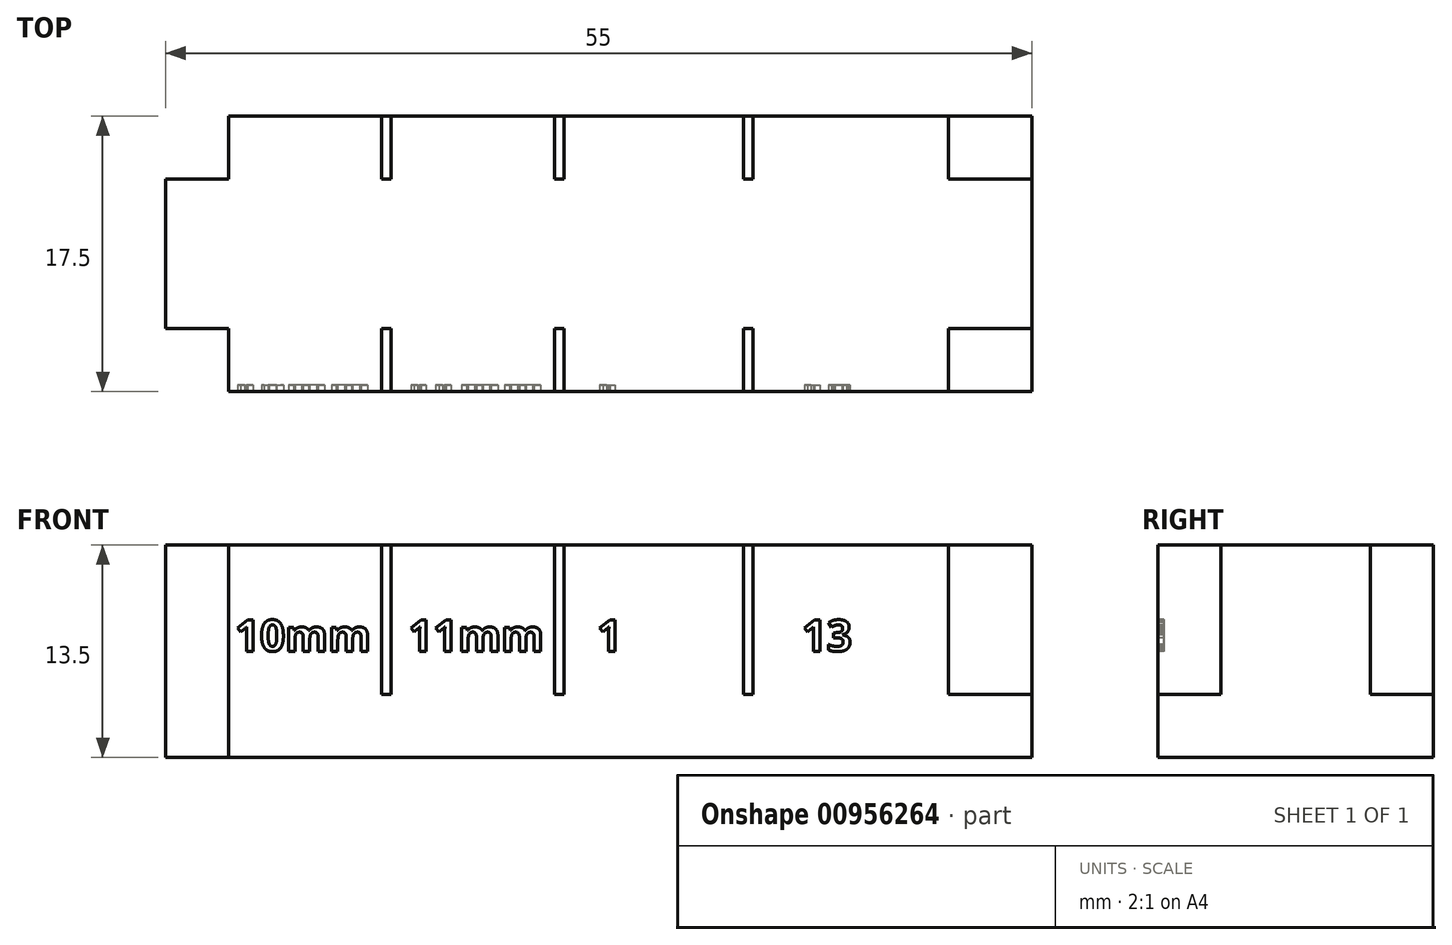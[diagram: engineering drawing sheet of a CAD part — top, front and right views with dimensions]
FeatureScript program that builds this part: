
annotation { "Feature Type Name" : "Feature", "Feature Type Description" : "" }
export const myFeature = defineFeature(function(context is Context, id is Id, definition is map)
    precondition{}
    {
        {
            var Q0;
            Q0=qCreatedBy(makeId("Top.planeOp"),FACE);
            var sketch = newSketch(context, id + "F0", { "sketchPlane" : qUnion([Q0])});
            skLineSegment(sketch, "E0.bottom", {"start": v(-8.23, -5.67) * mm, "end": v(46.77, -5.67) * mm});
            skLineSegment(sketch, "E0.top", {"start": v(-8.23, -23.17) * mm, "end": v(46.77, -23.17) * mm});
            skLineSegment(sketch, "E0.left", {"start": v(-8.23, -5.67) * mm, "end": v(-8.23, -23.17) * mm});
            skLineSegment(sketch, "E0.right", {"start": v(46.77, -5.67) * mm, "end": v(46.77, -23.17) * mm});
            skLineSegment(sketch, "E1.top", {"start": v(-8.23, -9.67) * mm, "end": v(46.77, -9.67) * mm});
            skLineSegment(sketch, "E1.left", {"start": v(-8.23, -5.67) * mm, "end": v(-8.23, -9.67) * mm});
            skLineSegment(sketch, "E1.right", {"start": v(46.77, -5.67) * mm, "end": v(46.77, -9.67) * mm});
            skLineSegment(sketch, "E2.top", {"start": v(-8.23, -19.17) * mm, "end": v(46.77, -19.17) * mm});
            skLineSegment(sketch, "E2.left", {"start": v(-8.23, -23.17) * mm, "end": v(-8.23, -19.17) * mm});
            skLineSegment(sketch, "E2.right", {"start": v(46.77, -23.17) * mm, "end": v(46.77, -19.17) * mm});
            skLineSegment(sketch, "E3.bottom", {"start": v(-8.23, -5.67) * mm, "end": v(-4.23, -5.67) * mm});
            skLineSegment(sketch, "E3.top", {"start": v(-8.23, -23.17) * mm, "end": v(-4.23, -23.17) * mm});
            skLineSegment(sketch, "E3.right", {"start": v(-4.23, -5.67) * mm, "end": v(-4.23, -23.17) * mm});
            skLineSegment(sketch, "E4", {"start": v(5.77, -5.67) * mm, "end": v(5.77, -23.17) * mm});
            skLineSegment(sketch, "E5", {"start": v(16.77, -5.67) * mm, "end": v(16.77, -23.17) * mm});
            skLineSegment(sketch, "E6", {"start": v(28.77, -5.67) * mm, "end": v(28.77, -23.17) * mm});
            skLineSegment(sketch, "E7", {"start": v(41.77, -5.67) * mm, "end": v(41.77, -23.17) * mm});
            skLineSegment(sketch, "E8.bottom", {"start": v(5.47, -5.67) * mm, "end": v(6.07, -5.67) * mm});
            skLineSegment(sketch, "E8.top", {"start": v(5.47, -23.17) * mm, "end": v(6.07, -23.17) * mm});
            skLineSegment(sketch, "E8.left", {"start": v(5.47, -5.67) * mm, "end": v(5.47, -23.17) * mm});
            skLineSegment(sketch, "E8.right", {"start": v(6.07, -5.67) * mm, "end": v(6.07, -23.17) * mm});
            skPoint(sketch, "E8.middle", {"position": v(5.77, -14.42) * mm});
            skLineSegment(sketch, "E9.bottom", {"start": v(16.47, -5.67) * mm, "end": v(17.07, -5.67) * mm});
            skLineSegment(sketch, "E9.top", {"start": v(16.47, -23.17) * mm, "end": v(17.07, -23.17) * mm});
            skLineSegment(sketch, "E9.left", {"start": v(16.47, -5.67) * mm, "end": v(16.47, -23.17) * mm});
            skLineSegment(sketch, "E9.right", {"start": v(17.07, -5.67) * mm, "end": v(17.07, -23.17) * mm});
            skPoint(sketch, "E9.middle", {"position": v(16.77, -14.42) * mm});
            skLineSegment(sketch, "E10.bottom", {"start": v(28.47, -5.67) * mm, "end": v(29.07, -5.67) * mm});
            skLineSegment(sketch, "E10.top", {"start": v(28.47, -23.17) * mm, "end": v(29.07, -23.17) * mm});
            skLineSegment(sketch, "E10.left", {"start": v(28.47, -5.67) * mm, "end": v(28.47, -23.17) * mm});
            skLineSegment(sketch, "E10.right", {"start": v(29.07, -5.67) * mm, "end": v(29.07, -23.17) * mm});
            skPoint(sketch, "E10.middle", {"position": v(28.77, -14.42) * mm});
            skLineSegment(sketch, "E11.bottom", {"start": v(41.47, -5.67) * mm, "end": v(42.07, -5.67) * mm});
            skLineSegment(sketch, "E11.top", {"start": v(41.47, -23.17) * mm, "end": v(42.07, -23.17) * mm});
            skLineSegment(sketch, "E11.left", {"start": v(41.47, -5.67) * mm, "end": v(41.47, -23.17) * mm});
            skLineSegment(sketch, "E11.right", {"start": v(42.07, -5.67) * mm, "end": v(42.07, -23.17) * mm});
            skPoint(sketch, "E11.middle", {"position": v(41.77, -14.42) * mm});
            skSolve(sketch);
        }
        {
            var Q0;
            {var subQ0=sQuery(id+"F0.wireOp",EDGE,"E3.right");var subQ1=sQuery(id+"F0.wireOp",EDGE,"E1.top");var subQ2=makeQuery(id+"F0.imprint","INTERSECT",VERTEX,{"derivedFrom":[subQ1,subQ0]});Q0=makeQuery(id+"F0.imprint","IMPRINT",FACE,{"disambiguationData":[TD([[makeQuery(id+"F0.imprint","IMPRINT",EDGE,{"disambiguationData":[TD([[subQ2,-1.0]])],"derivedFrom":subQ1}),-1.0]])]});}
            var Q1;
            {var subQ0=sQuery(id+"F0.wireOp",EDGE,"E8.left");var subQ1=sQuery(id+"F0.wireOp",EDGE,"E1.top");var subQ2=makeQuery(id+"F0.imprint","INTERSECT",VERTEX,{"derivedFrom":[subQ1,subQ0]});Q1=makeQuery(id+"F0.imprint","IMPRINT",FACE,{"disambiguationData":[TD([[makeQuery(id+"F0.imprint","IMPRINT",EDGE,{"disambiguationData":[TD([[subQ2,-1.0]])],"derivedFrom":subQ1}),-1.0]])]});}
            var Q2;
            {var subQ0=sQuery(id+"F0.wireOp",EDGE,"E4");var subQ1=sQuery(id+"F0.wireOp",EDGE,"E1.top");var subQ2=makeQuery(id+"F0.imprint","INTERSECT",VERTEX,{"derivedFrom":[subQ1,subQ0]});Q2=makeQuery(id+"F0.imprint","IMPRINT",FACE,{"disambiguationData":[TD([[makeQuery(id+"F0.imprint","IMPRINT",EDGE,{"disambiguationData":[TD([[subQ2,-1.0]])],"derivedFrom":subQ1}),-1.0]])]});}
            var Q3;
            {var subQ0=sQuery(id+"F0.wireOp",EDGE,"E8.right");var subQ1=sQuery(id+"F0.wireOp",EDGE,"E1.top");var subQ2=makeQuery(id+"F0.imprint","INTERSECT",VERTEX,{"derivedFrom":[subQ1,subQ0]});Q3=makeQuery(id+"F0.imprint","IMPRINT",FACE,{"disambiguationData":[TD([[makeQuery(id+"F0.imprint","IMPRINT",EDGE,{"disambiguationData":[TD([[subQ2,-1.0]])],"derivedFrom":subQ1}),-1.0]])]});}
            var Q4;
            {var subQ0=sQuery(id+"F0.wireOp",EDGE,"E9.left");var subQ1=sQuery(id+"F0.wireOp",EDGE,"E1.top");var subQ2=makeQuery(id+"F0.imprint","INTERSECT",VERTEX,{"derivedFrom":[subQ1,subQ0]});Q4=makeQuery(id+"F0.imprint","IMPRINT",FACE,{"disambiguationData":[TD([[makeQuery(id+"F0.imprint","IMPRINT",EDGE,{"disambiguationData":[TD([[subQ2,-1.0]])],"derivedFrom":subQ1}),-1.0]])]});}
            var Q5;
            {var subQ0=sQuery(id+"F0.wireOp",EDGE,"E5");var subQ1=sQuery(id+"F0.wireOp",EDGE,"E1.top");var subQ2=makeQuery(id+"F0.imprint","INTERSECT",VERTEX,{"derivedFrom":[subQ1,subQ0]});Q5=makeQuery(id+"F0.imprint","IMPRINT",FACE,{"disambiguationData":[TD([[makeQuery(id+"F0.imprint","IMPRINT",EDGE,{"disambiguationData":[TD([[subQ2,-1.0]])],"derivedFrom":subQ1}),-1.0]])]});}
            var Q6;
            {var subQ0=sQuery(id+"F0.wireOp",EDGE,"E9.right");var subQ1=sQuery(id+"F0.wireOp",EDGE,"E1.top");var subQ2=makeQuery(id+"F0.imprint","INTERSECT",VERTEX,{"derivedFrom":[subQ1,subQ0]});Q6=makeQuery(id+"F0.imprint","IMPRINT",FACE,{"disambiguationData":[TD([[makeQuery(id+"F0.imprint","IMPRINT",EDGE,{"disambiguationData":[TD([[subQ2,-1.0]])],"derivedFrom":subQ1}),-1.0]])]});}
            var Q7;
            {var subQ0=sQuery(id+"F0.wireOp",EDGE,"E10.left");var subQ1=sQuery(id+"F0.wireOp",EDGE,"E1.top");var subQ2=makeQuery(id+"F0.imprint","INTERSECT",VERTEX,{"derivedFrom":[subQ1,subQ0]});Q7=makeQuery(id+"F0.imprint","IMPRINT",FACE,{"disambiguationData":[TD([[makeQuery(id+"F0.imprint","IMPRINT",EDGE,{"disambiguationData":[TD([[subQ2,-1.0]])],"derivedFrom":subQ1}),-1.0]])]});}
            var Q8;
            {var subQ0=sQuery(id+"F0.wireOp",EDGE,"E6");var subQ1=sQuery(id+"F0.wireOp",EDGE,"E1.top");var subQ2=makeQuery(id+"F0.imprint","INTERSECT",VERTEX,{"derivedFrom":[subQ1,subQ0]});Q8=makeQuery(id+"F0.imprint","IMPRINT",FACE,{"disambiguationData":[TD([[makeQuery(id+"F0.imprint","IMPRINT",EDGE,{"disambiguationData":[TD([[subQ2,-1.0]])],"derivedFrom":subQ1}),-1.0]])]});}
            var Q9;
            {var subQ0=sQuery(id+"F0.wireOp",EDGE,"E10.right");var subQ1=sQuery(id+"F0.wireOp",EDGE,"E1.top");var subQ2=makeQuery(id+"F0.imprint","INTERSECT",VERTEX,{"derivedFrom":[subQ1,subQ0]});Q9=makeQuery(id+"F0.imprint","IMPRINT",FACE,{"disambiguationData":[TD([[makeQuery(id+"F0.imprint","IMPRINT",EDGE,{"disambiguationData":[TD([[subQ2,-1.0]])],"derivedFrom":subQ1}),-1.0]])]});}
            var Q10;
            {var subQ0=sQuery(id+"F0.wireOp",EDGE,"E11.left");var subQ1=sQuery(id+"F0.wireOp",EDGE,"E1.top");var subQ2=makeQuery(id+"F0.imprint","INTERSECT",VERTEX,{"derivedFrom":[subQ1,subQ0]});Q10=makeQuery(id+"F0.imprint","IMPRINT",FACE,{"disambiguationData":[TD([[makeQuery(id+"F0.imprint","IMPRINT",EDGE,{"disambiguationData":[TD([[subQ2,-1.0]])],"derivedFrom":subQ1}),-1.0]])]});}
            var Q11;
            {var subQ0=sQuery(id+"F0.wireOp",EDGE,"E7");var subQ1=sQuery(id+"F0.wireOp",EDGE,"E1.top");var subQ2=makeQuery(id+"F0.imprint","INTERSECT",VERTEX,{"derivedFrom":[subQ1,subQ0]});Q11=makeQuery(id+"F0.imprint","IMPRINT",FACE,{"disambiguationData":[TD([[makeQuery(id+"F0.imprint","IMPRINT",EDGE,{"disambiguationData":[TD([[subQ2,-1.0]])],"derivedFrom":subQ1}),-1.0]])]});}
            var Q12;
            {var subQ0=sQuery(id+"F0.wireOp",EDGE,"E0.right");Q12=makeQuery(id+"F0.imprint","IMPRINT",FACE,{"disambiguationData":[TD([[makeQuery(id+"F0.imprint","IMPRINT",EDGE,{"derivedFrom":subQ0}),-1.0]])]});}
            var Q13;
            {var subQ0=sQuery(id+"F0.wireOp",EDGE,"E7");var subQ1=sQuery(id+"F0.wireOp",EDGE,"E1.top");var subQ2=makeQuery(id+"F0.imprint","INTERSECT",VERTEX,{"derivedFrom":[subQ1,subQ0]});Q13=makeQuery(id+"F0.imprint","IMPRINT",FACE,{"disambiguationData":[TD([[makeQuery(id+"F0.imprint","IMPRINT",EDGE,{"disambiguationData":[TD([[subQ2,-1.0]])],"derivedFrom":subQ1}),1.0]])]});}
            var Q14;
            {var subQ0=sQuery(id+"F0.wireOp",EDGE,"E11.left");var subQ1=sQuery(id+"F0.wireOp",EDGE,"E1.top");var subQ2=makeQuery(id+"F0.imprint","INTERSECT",VERTEX,{"derivedFrom":[subQ1,subQ0]});Q14=makeQuery(id+"F0.imprint","IMPRINT",FACE,{"disambiguationData":[TD([[makeQuery(id+"F0.imprint","IMPRINT",EDGE,{"disambiguationData":[TD([[subQ2,-1.0]])],"derivedFrom":subQ1}),1.0]])]});}
            var Q15;
            {var subQ0=sQuery(id+"F0.wireOp",EDGE,"E6");var subQ1=sQuery(id+"F0.wireOp",EDGE,"E1.top");var subQ2=makeQuery(id+"F0.imprint","INTERSECT",VERTEX,{"derivedFrom":[subQ1,subQ0]});Q15=makeQuery(id+"F0.imprint","IMPRINT",FACE,{"disambiguationData":[TD([[makeQuery(id+"F0.imprint","IMPRINT",EDGE,{"disambiguationData":[TD([[subQ2,-1.0]])],"derivedFrom":subQ1}),1.0]])]});}
            var Q16;
            {var subQ0=sQuery(id+"F0.wireOp",EDGE,"E10.left");var subQ1=sQuery(id+"F0.wireOp",EDGE,"E1.top");var subQ2=makeQuery(id+"F0.imprint","INTERSECT",VERTEX,{"derivedFrom":[subQ1,subQ0]});Q16=makeQuery(id+"F0.imprint","IMPRINT",FACE,{"disambiguationData":[TD([[makeQuery(id+"F0.imprint","IMPRINT",EDGE,{"disambiguationData":[TD([[subQ2,-1.0]])],"derivedFrom":subQ1}),1.0]])]});}
            var Q17;
            {var subQ0=sQuery(id+"F0.wireOp",EDGE,"E5");var subQ1=sQuery(id+"F0.wireOp",EDGE,"E1.top");var subQ2=makeQuery(id+"F0.imprint","INTERSECT",VERTEX,{"derivedFrom":[subQ1,subQ0]});Q17=makeQuery(id+"F0.imprint","IMPRINT",FACE,{"disambiguationData":[TD([[makeQuery(id+"F0.imprint","IMPRINT",EDGE,{"disambiguationData":[TD([[subQ2,-1.0]])],"derivedFrom":subQ1}),1.0]])]});}
            var Q18;
            {var subQ0=sQuery(id+"F0.wireOp",EDGE,"E9.left");var subQ1=sQuery(id+"F0.wireOp",EDGE,"E1.top");var subQ2=makeQuery(id+"F0.imprint","INTERSECT",VERTEX,{"derivedFrom":[subQ1,subQ0]});Q18=makeQuery(id+"F0.imprint","IMPRINT",FACE,{"disambiguationData":[TD([[makeQuery(id+"F0.imprint","IMPRINT",EDGE,{"disambiguationData":[TD([[subQ2,-1.0]])],"derivedFrom":subQ1}),1.0]])]});}
            var Q19;
            {var subQ0=sQuery(id+"F0.wireOp",EDGE,"E4");var subQ1=sQuery(id+"F0.wireOp",EDGE,"E1.top");var subQ2=makeQuery(id+"F0.imprint","INTERSECT",VERTEX,{"derivedFrom":[subQ1,subQ0]});Q19=makeQuery(id+"F0.imprint","IMPRINT",FACE,{"disambiguationData":[TD([[makeQuery(id+"F0.imprint","IMPRINT",EDGE,{"disambiguationData":[TD([[subQ2,-1.0]])],"derivedFrom":subQ1}),1.0]])]});}
            var Q20;
            {var subQ0=sQuery(id+"F0.wireOp",EDGE,"E8.left");var subQ1=sQuery(id+"F0.wireOp",EDGE,"E1.top");var subQ2=makeQuery(id+"F0.imprint","INTERSECT",VERTEX,{"derivedFrom":[subQ1,subQ0]});Q20=makeQuery(id+"F0.imprint","IMPRINT",FACE,{"disambiguationData":[TD([[makeQuery(id+"F0.imprint","IMPRINT",EDGE,{"disambiguationData":[TD([[subQ2,-1.0]])],"derivedFrom":subQ1}),1.0]])]});}
            var Q21;
            {var subQ0=sQuery(id+"F0.wireOp",EDGE,"E8.left");var subQ1=sQuery(id+"F0.wireOp",EDGE,"E2.top");var subQ2=makeQuery(id+"F0.imprint","INTERSECT",VERTEX,{"derivedFrom":[subQ1,subQ0]});Q21=makeQuery(id+"F0.imprint","IMPRINT",FACE,{"disambiguationData":[TD([[makeQuery(id+"F0.imprint","IMPRINT",EDGE,{"disambiguationData":[TD([[subQ2,-1.0]])],"derivedFrom":subQ1}),-1.0]])]});}
            var Q22;
            {var subQ0=sQuery(id+"F0.wireOp",EDGE,"E4");var subQ1=sQuery(id+"F0.wireOp",EDGE,"E2.top");var subQ2=makeQuery(id+"F0.imprint","INTERSECT",VERTEX,{"derivedFrom":[subQ1,subQ0]});Q22=makeQuery(id+"F0.imprint","IMPRINT",FACE,{"disambiguationData":[TD([[makeQuery(id+"F0.imprint","IMPRINT",EDGE,{"disambiguationData":[TD([[subQ2,-1.0]])],"derivedFrom":subQ1}),-1.0]])]});}
            var Q23;
            {var subQ0=sQuery(id+"F0.wireOp",EDGE,"E9.left");var subQ1=sQuery(id+"F0.wireOp",EDGE,"E2.top");var subQ2=makeQuery(id+"F0.imprint","INTERSECT",VERTEX,{"derivedFrom":[subQ1,subQ0]});Q23=makeQuery(id+"F0.imprint","IMPRINT",FACE,{"disambiguationData":[TD([[makeQuery(id+"F0.imprint","IMPRINT",EDGE,{"disambiguationData":[TD([[subQ2,-1.0]])],"derivedFrom":subQ1}),-1.0]])]});}
            var Q24;
            {var subQ0=sQuery(id+"F0.wireOp",EDGE,"E5");var subQ1=sQuery(id+"F0.wireOp",EDGE,"E2.top");var subQ2=makeQuery(id+"F0.imprint","INTERSECT",VERTEX,{"derivedFrom":[subQ1,subQ0]});Q24=makeQuery(id+"F0.imprint","IMPRINT",FACE,{"disambiguationData":[TD([[makeQuery(id+"F0.imprint","IMPRINT",EDGE,{"disambiguationData":[TD([[subQ2,-1.0]])],"derivedFrom":subQ1}),-1.0]])]});}
            var Q25;
            {var subQ0=sQuery(id+"F0.wireOp",EDGE,"E10.left");var subQ1=sQuery(id+"F0.wireOp",EDGE,"E2.top");var subQ2=makeQuery(id+"F0.imprint","INTERSECT",VERTEX,{"derivedFrom":[subQ1,subQ0]});Q25=makeQuery(id+"F0.imprint","IMPRINT",FACE,{"disambiguationData":[TD([[makeQuery(id+"F0.imprint","IMPRINT",EDGE,{"disambiguationData":[TD([[subQ2,-1.0]])],"derivedFrom":subQ1}),-1.0]])]});}
            var Q26;
            {var subQ0=sQuery(id+"F0.wireOp",EDGE,"E6");var subQ1=sQuery(id+"F0.wireOp",EDGE,"E2.top");var subQ2=makeQuery(id+"F0.imprint","INTERSECT",VERTEX,{"derivedFrom":[subQ1,subQ0]});Q26=makeQuery(id+"F0.imprint","IMPRINT",FACE,{"disambiguationData":[TD([[makeQuery(id+"F0.imprint","IMPRINT",EDGE,{"disambiguationData":[TD([[subQ2,-1.0]])],"derivedFrom":subQ1}),-1.0]])]});}
            var Q27;
            {var subQ0=sQuery(id+"F0.wireOp",EDGE,"E11.left");var subQ1=sQuery(id+"F0.wireOp",EDGE,"E2.top");var subQ2=makeQuery(id+"F0.imprint","INTERSECT",VERTEX,{"derivedFrom":[subQ1,subQ0]});Q27=makeQuery(id+"F0.imprint","IMPRINT",FACE,{"disambiguationData":[TD([[makeQuery(id+"F0.imprint","IMPRINT",EDGE,{"disambiguationData":[TD([[subQ2,-1.0]])],"derivedFrom":subQ1}),-1.0]])]});}
            var Q28;
            {var subQ0=sQuery(id+"F0.wireOp",EDGE,"E7");var subQ1=sQuery(id+"F0.wireOp",EDGE,"E2.top");var subQ2=makeQuery(id+"F0.imprint","INTERSECT",VERTEX,{"derivedFrom":[subQ1,subQ0]});Q28=makeQuery(id+"F0.imprint","IMPRINT",FACE,{"disambiguationData":[TD([[makeQuery(id+"F0.imprint","IMPRINT",EDGE,{"disambiguationData":[TD([[subQ2,-1.0]])],"derivedFrom":subQ1}),-1.0]])]});}
            extrude(context, id + "F1", {"entities" : qUnion([Q0, Q1, Q2, Q3, Q4, Q5, Q6, Q7, Q8, Q9, Q10, Q11, Q12, Q13, Q14, Q15, Q16, Q17, Q18, Q19, Q20, Q21, Q22, Q23, Q24, Q25, Q26, Q27, Q28]), "depth" : 4 * mm, "offsetDistance" : 25 * mm});
        }
        {
            var Q0;
            {var subQ5=sQuery(id+"F0.wireOp",EDGE,"E3.bottom");Q0=makeQuery(id+"F0.imprint","IMPRINT",FACE,{"disambiguationData":[TD([[makeQuery(id+"F0.imprint","IMPRINT",EDGE,{"derivedFrom":subQ5}),-1.0]])]});}
            var Q1;
            {var subQ0=sQuery(id+"F0.wireOp",EDGE,"E0.left");var subQ1=sQuery(id+"F0.wireOp",EDGE,"E1.top");var subQ2=makeQuery(id+"F0.imprint","INTERSECT",VERTEX,{"derivedFrom":[subQ1,subQ0]});Q1=makeQuery(id+"F0.imprint","IMPRINT",FACE,{"disambiguationData":[TD([[makeQuery(id+"F0.imprint","IMPRINT",EDGE,{"disambiguationData":[TD([[subQ2,-1.0]])],"derivedFrom":subQ1}),-1.0]])]});}
            var Q2;
            {var subQ5=sQuery(id+"F0.wireOp",EDGE,"E3.top");Q2=makeQuery(id+"F0.imprint","IMPRINT",FACE,{"disambiguationData":[TD([[makeQuery(id+"F0.imprint","IMPRINT",EDGE,{"derivedFrom":subQ5}),1.0]])]});}
            var Q3;
            {var subQ0=sQuery(id+"F0.wireOp",EDGE,"E8.right");var subQ5=sQuery(id+"F0.wireOp",EDGE,"E2.top");var subQ7=makeQuery(id+"F0.imprint","INTERSECT",VERTEX,{"derivedFrom":[subQ5,subQ0]});Q3=makeQuery(id+"F0.imprint","IMPRINT",FACE,{"disambiguationData":[TD([[makeQuery(id+"F0.imprint","IMPRINT",EDGE,{"disambiguationData":[TD([[subQ7,-1.0]])],"derivedFrom":subQ5}),-1.0]])]});}
            var Q4;
            {var subQ0=sQuery(id+"F0.wireOp",EDGE,"E9.right");var subQ5=sQuery(id+"F0.wireOp",EDGE,"E2.top");var subQ6=makeQuery(id+"F0.imprint","INTERSECT",VERTEX,{"derivedFrom":[subQ5,subQ0]});Q4=makeQuery(id+"F0.imprint","IMPRINT",FACE,{"disambiguationData":[TD([[makeQuery(id+"F0.imprint","IMPRINT",EDGE,{"disambiguationData":[TD([[subQ6,-1.0]])],"derivedFrom":subQ5}),-1.0]])]});}
            var Q5;
            {var subQ0=sQuery(id+"F0.wireOp",EDGE,"E10.right");var subQ5=sQuery(id+"F0.wireOp",EDGE,"E2.top");var subQ6=makeQuery(id+"F0.imprint","INTERSECT",VERTEX,{"derivedFrom":[subQ5,subQ0]});Q5=makeQuery(id+"F0.imprint","IMPRINT",FACE,{"disambiguationData":[TD([[makeQuery(id+"F0.imprint","IMPRINT",EDGE,{"disambiguationData":[TD([[subQ6,-1.0]])],"derivedFrom":subQ5}),-1.0]])]});}
            var Q6;
            {var subQ0=sQuery(id+"F0.wireOp",EDGE,"E2.right");Q6=makeQuery(id+"F0.imprint","IMPRINT",FACE,{"disambiguationData":[TD([[makeQuery(id+"F0.imprint","IMPRINT",EDGE,{"derivedFrom":subQ0}),1.0]])]});}
            var Q7;
            {var subQ0=sQuery(id+"F0.wireOp",EDGE,"E1.right");Q7=makeQuery(id+"F0.imprint","IMPRINT",FACE,{"disambiguationData":[TD([[makeQuery(id+"F0.imprint","IMPRINT",EDGE,{"derivedFrom":subQ0}),-1.0]])]});}
            var Q8;
            {var subQ0=sQuery(id+"F0.wireOp",EDGE,"E10.right");var subQ5=sQuery(id+"F0.wireOp",EDGE,"E1.top");var subQ6=makeQuery(id+"F0.imprint","INTERSECT",VERTEX,{"derivedFrom":[subQ5,subQ0]});Q8=makeQuery(id+"F0.imprint","IMPRINT",FACE,{"disambiguationData":[TD([[makeQuery(id+"F0.imprint","IMPRINT",EDGE,{"disambiguationData":[TD([[subQ6,-1.0]])],"derivedFrom":subQ5}),1.0]])]});}
            var Q9;
            {var subQ0=sQuery(id+"F0.wireOp",EDGE,"E9.right");var subQ5=sQuery(id+"F0.wireOp",EDGE,"E1.top");var subQ6=makeQuery(id+"F0.imprint","INTERSECT",VERTEX,{"derivedFrom":[subQ5,subQ0]});Q9=makeQuery(id+"F0.imprint","IMPRINT",FACE,{"disambiguationData":[TD([[makeQuery(id+"F0.imprint","IMPRINT",EDGE,{"disambiguationData":[TD([[subQ6,-1.0]])],"derivedFrom":subQ5}),1.0]])]});}
            var Q10;
            {var subQ0=sQuery(id+"F0.wireOp",EDGE,"E8.right");var subQ5=sQuery(id+"F0.wireOp",EDGE,"E1.top");var subQ6=makeQuery(id+"F0.imprint","INTERSECT",VERTEX,{"derivedFrom":[subQ5,subQ0]});Q10=makeQuery(id+"F0.imprint","IMPRINT",FACE,{"disambiguationData":[TD([[makeQuery(id+"F0.imprint","IMPRINT",EDGE,{"disambiguationData":[TD([[subQ6,-1.0]])],"derivedFrom":subQ5}),1.0]])]});}
            var Q11;
            {var subQ0=sQuery(id+"F0.wireOp",EDGE,"E3.right");var subQ5=sQuery(id+"F0.wireOp",EDGE,"E1.top");var subQ6=makeQuery(id+"F0.imprint","INTERSECT",VERTEX,{"derivedFrom":[subQ5,subQ0]});Q11=makeQuery(id+"F0.imprint","IMPRINT",FACE,{"disambiguationData":[TD([[makeQuery(id+"F0.imprint","IMPRINT",EDGE,{"disambiguationData":[TD([[subQ6,-1.0]])],"derivedFrom":subQ5}),1.0]])]});}
            var Q12;
            {var subQ0=sQuery(id+"F0.wireOp",EDGE,"E3.right");var subQ5=sQuery(id+"F0.wireOp",EDGE,"E2.top");var subQ6=makeQuery(id+"F0.imprint","INTERSECT",VERTEX,{"derivedFrom":[subQ5,subQ0]});Q12=makeQuery(id+"F0.imprint","IMPRINT",FACE,{"disambiguationData":[TD([[makeQuery(id+"F0.imprint","IMPRINT",EDGE,{"disambiguationData":[TD([[subQ6,-1.0]])],"derivedFrom":subQ5}),-1.0]])]});}
            extrude(context, id + "F2", {"entities" : qUnion([Q0, Q1, Q2, Q3, Q4, Q5, Q6, Q7, Q8, Q9, Q10, Q11, Q12]), "operationType" : NewBodyOperationType.ADD, "depth" : 13.5 * mm, "offsetDistance" : 25 * mm});
        }
        {
            var Q0;
            {var subQ0=sQuery(id+"F0.wireOp",EDGE,"E0.top");var subQ1=sQuery(id+"F0.wireOp",EDGE,"E11.top");var subQ2=sQuery(id+"F0.wireOp",EDGE,"E10.top");var subQ3=sQuery(id+"F0.wireOp",EDGE,"E9.top");var subQ4=sQuery(id+"F0.wireOp",EDGE,"E8.top");Q0=makeQuery(id+"F2.boolean.opBoolean","MERGE",FACE,{"derivedFrom":[makeQuery(id+"F1.opExtrude","SWEPT_FACE",FACE,{"disambiguationData":[OSD([subQ4])]}),makeQuery(id+"F1.opExtrude","SWEPT_FACE",FACE,{"disambiguationData":[OSD([subQ3])]}),makeQuery(id+"F1.opExtrude","SWEPT_FACE",FACE,{"disambiguationData":[OSD([subQ2])]}),makeQuery(id+"F1.opExtrude","SWEPT_FACE",FACE,{"disambiguationData":[OSD([subQ1])]}),makeQuery(id+"F2.opExtrude","SWEPT_FACE",FACE,{"disambiguationData":[OSD([subQ0,sQuery(id+"F0.wireOp",EDGE,"E3.top")])]}),makeQuery(id+"F2.opExtrude","SWEPT_FACE",FACE,{"disambiguationData":[OSD([subQ0]),TDD([makeQuery(id+"F0.imprint","IMPRINT",EDGE,{"disambiguationData":[TD([[makeQuery(id+"F0.imprint","INTERSECT",VERTEX,{"derivedFrom":[subQ0,subQ4,sQuery(id+"F0.wireOp",EDGE,"E8.right")]}),-1.0]])],"derivedFrom":subQ0})])]}),makeQuery(id+"F2.opExtrude","SWEPT_FACE",FACE,{"disambiguationData":[OSD([subQ0]),TDD([makeQuery(id+"F0.imprint","IMPRINT",EDGE,{"disambiguationData":[TD([[makeQuery(id+"F0.imprint","INTERSECT",VERTEX,{"derivedFrom":[subQ0,subQ3,sQuery(id+"F0.wireOp",EDGE,"E9.right")]}),-1.0]])],"derivedFrom":subQ0})])]}),makeQuery(id+"F2.opExtrude","SWEPT_FACE",FACE,{"disambiguationData":[OSD([subQ0]),TDD([makeQuery(id+"F0.imprint","IMPRINT",EDGE,{"disambiguationData":[TD([[makeQuery(id+"F0.imprint","INTERSECT",VERTEX,{"derivedFrom":[subQ0,subQ2,sQuery(id+"F0.wireOp",EDGE,"E10.right")]}),-1.0]])],"derivedFrom":subQ0})])]}),makeQuery(id+"F2.opExtrude","SWEPT_FACE",FACE,{"disambiguationData":[OSD([subQ0]),TDD([makeQuery(id+"F0.imprint","IMPRINT",EDGE,{"disambiguationData":[TD([[makeQuery(id+"F0.imprint","INTERSECT",VERTEX,{"derivedFrom":[subQ0,sQuery(id+"F0.wireOp",EDGE,"E2.right")]}),1.0]])],"derivedFrom":subQ0})])]})]});}
            var sketch = newSketch(context, id + "F3", { "sketchPlane" : qUnion([Q0])});
            skText(sketch, "E12", { "text": "10mm\n", "fontName": "OpenSans-Bold.ttf"});
            skPoint(sketch, "E12.firstSnap0", {"position": v(-3.83, 13.35) * mm});
            skText(sketch, "E13", { "text": "11mm", "fontName": "OpenSans-Bold.ttf"});
            skLineSegment(sketch, "E14", {"start": v(-8.23, 6.75) * mm, "end": v(46.77, 6.75) * mm});
            skText(sketch, "E15", { "text": "12mm", "fontName": "OpenSans-Bold.ttf"});
            skText(sketch, "E16", { "text": "13mm\n", "fontName": "OpenSans-Bold.ttf"});
            const initialGuessF3  = {"E12": [-0.00383, 0.00675, 1, 0, 0.002], "E13": [0.00717, 0.00675, 1, 0, 0.002], "E15": [0.01917, 0.00675, 1, 0, 0.002], "E16": [0.03217, 0.00675, 1, 0, 0.002]};
            skSetInitialGuess(sketch, initialGuessF3);
            skSolve(sketch);
        }
        {
            var Q0;
            {var subQ0=sQuery(id+"F3.wireOp",EDGE,"E12.sketch_text.stroke-1");Q0=makeQuery(id+"F3.imprint","IMPRINT",FACE,{"disambiguationData":[TD([[makeQuery(id+"F3.imprint","IMPRINT",EDGE,{"derivedFrom":subQ0}),-1.0]])]});}
            var Q1;
            {var subQ0=sQuery(id+"F3.wireOp",EDGE,"E12.sketch_text.stroke-9");Q1=makeQuery(id+"F3.imprint","IMPRINT",FACE,{"disambiguationData":[TD([[makeQuery(id+"F3.imprint","IMPRINT",EDGE,{"derivedFrom":subQ0}),-1.0]])]});}
            var Q2;
            {var subQ2=sQuery(id+"F3.wireOp",EDGE,"E12.sketch_text.stroke-25");Q2=makeQuery(id+"F3.imprint","IMPRINT",FACE,{"disambiguationData":[TD([[makeQuery(id+"F3.imprint","IMPRINT",EDGE,{"derivedFrom":subQ2}),-1.0]])]});}
            var Q3;
            {var subQ2=sQuery(id+"F3.wireOp",EDGE,"E12.sketch_text.stroke-53");Q3=makeQuery(id+"F3.imprint","IMPRINT",FACE,{"disambiguationData":[TD([[makeQuery(id+"F3.imprint","IMPRINT",EDGE,{"derivedFrom":subQ2}),-1.0]])]});}
            var Q4;
            {var subQ0=sQuery(id+"F3.wireOp",EDGE,"E13.sketch_text.stroke-1");Q4=makeQuery(id+"F3.imprint","IMPRINT",FACE,{"disambiguationData":[TD([[makeQuery(id+"F3.imprint","IMPRINT",EDGE,{"derivedFrom":subQ0}),-1.0]])]});}
            var Q5;
            {var subQ1=sQuery(id+"F3.wireOp",EDGE,"E13.sketch_text.stroke-10");Q5=makeQuery(id+"F3.imprint","IMPRINT",FACE,{"disambiguationData":[TD([[makeQuery(id+"F3.imprint","IMPRINT",EDGE,{"derivedFrom":subQ1}),-1.0]])]});}
            var Q6;
            {var subQ2=sQuery(id+"F3.wireOp",EDGE,"E13.sketch_text.stroke-18");Q6=makeQuery(id+"F3.imprint","IMPRINT",FACE,{"disambiguationData":[TD([[makeQuery(id+"F3.imprint","IMPRINT",EDGE,{"derivedFrom":subQ2}),-1.0]])]});}
            var Q7;
            {var subQ3=sQuery(id+"F3.wireOp",EDGE,"E13.sketch_text.stroke-46");Q7=makeQuery(id+"F3.imprint","IMPRINT",FACE,{"disambiguationData":[TD([[makeQuery(id+"F3.imprint","IMPRINT",EDGE,{"derivedFrom":subQ3}),-1.0]])]});}
            var Q8;
            Q8=makeQuery(id+"F3.imprint","IMPRINT",FACE,{"disambiguationData":[TD([[makeQuery(id+"F3.imprint","IMPRINT",EDGE,{"derivedFrom":sQuery(id+"F3.wireOp",EDGE,"E15.sketch_text.stroke-0")}),-1.0]])]});
            var Q9;
            Q9=makeQuery(id+"F3.imprint","IMPRINT",FACE,{"disambiguationData":[TD([[makeQuery(id+"F3.imprint","IMPRINT",EDGE,{"derivedFrom":sQuery(id+"F3.wireOp",EDGE,"E15.sketch_text.stroke-9")}),-1.0]])]});
            var Q10;
            Q10=makeQuery(id+"F3.imprint","IMPRINT",FACE,{"disambiguationData":[TD([[makeQuery(id+"F3.imprint","IMPRINT",EDGE,{"derivedFrom":sQuery(id+"F3.wireOp",EDGE,"E15.sketch_text.stroke-29")}),-1.0]])]});
            var Q11;
            Q11=makeQuery(id+"F3.imprint","IMPRINT",FACE,{"disambiguationData":[TD([[makeQuery(id+"F3.imprint","IMPRINT",EDGE,{"derivedFrom":sQuery(id+"F3.wireOp",EDGE,"E15.sketch_text.stroke-57")}),-1.0]])]});
            var Q12;
            Q12=makeQuery(id+"F3.imprint","IMPRINT",FACE,{"disambiguationData":[TD([[makeQuery(id+"F3.imprint","IMPRINT",EDGE,{"derivedFrom":sQuery(id+"F3.wireOp",EDGE,"E16.sketch_text.stroke-65")}),-1.0]])]});
            var Q13;
            Q13=makeQuery(id+"F3.imprint","IMPRINT",FACE,{"disambiguationData":[TD([[makeQuery(id+"F3.imprint","IMPRINT",EDGE,{"derivedFrom":sQuery(id+"F3.wireOp",EDGE,"E16.sketch_text.stroke-37")}),-1.0]])]});
            var Q14;
            Q14=makeQuery(id+"F3.imprint","IMPRINT",FACE,{"disambiguationData":[TD([[makeQuery(id+"F3.imprint","IMPRINT",EDGE,{"derivedFrom":sQuery(id+"F3.wireOp",EDGE,"E16.sketch_text.stroke-9")}),-1.0]])]});
            var Q15;
            Q15=makeQuery(id+"F3.imprint","IMPRINT",FACE,{"disambiguationData":[TD([[makeQuery(id+"F3.imprint","IMPRINT",EDGE,{"derivedFrom":sQuery(id+"F3.wireOp",EDGE,"E16.sketch_text.stroke-0")}),-1.0]])]});
            var Q16;
            {var subQ3=sQuery(id+"F3.wireOp",EDGE,"E12.sketch_text.stroke-55");Q16=makeQuery(id+"F3.imprint","IMPRINT",FACE,{"disambiguationData":[TD([[makeQuery(id+"F3.imprint","IMPRINT",EDGE,{"derivedFrom":subQ3}),-1.0]])]});}
            var Q17;
            {var subQ3=sQuery(id+"F3.wireOp",EDGE,"E13.sketch_text.stroke-49");Q17=makeQuery(id+"F3.imprint","IMPRINT",FACE,{"disambiguationData":[TD([[makeQuery(id+"F3.imprint","IMPRINT",EDGE,{"derivedFrom":subQ3}),-1.0]])]});}
            var Q18;
            Q18=makeQuery(id+"F3.imprint","IMPRINT",FACE,{"disambiguationData":[TD([[makeQuery(id+"F3.imprint","IMPRINT",EDGE,{"derivedFrom":sQuery(id+"F3.wireOp",EDGE,"E15.sketch_text.stroke-62")}),-1.0]])]});
            var Q19;
            Q19=makeQuery(id+"F3.imprint","IMPRINT",FACE,{"disambiguationData":[TD([[makeQuery(id+"F3.imprint","IMPRINT",EDGE,{"derivedFrom":sQuery(id+"F3.wireOp",EDGE,"E16.sketch_text.stroke-10")}),-1.0]])]});
            extrude(context, id + "F4", {"entities" : qUnion([Q0, Q1, Q2, Q3, Q4, Q5, Q6, Q7, Q8, Q9, Q10, Q11, Q12, Q13, Q14, Q15, Q16, Q17, Q18, Q19]), "operationType" : NewBodyOperationType.REMOVE, "oppositeDirection" : true, "depth" : 0.4 * mm, "offsetDistance" : 25 * mm});
        }
    });
